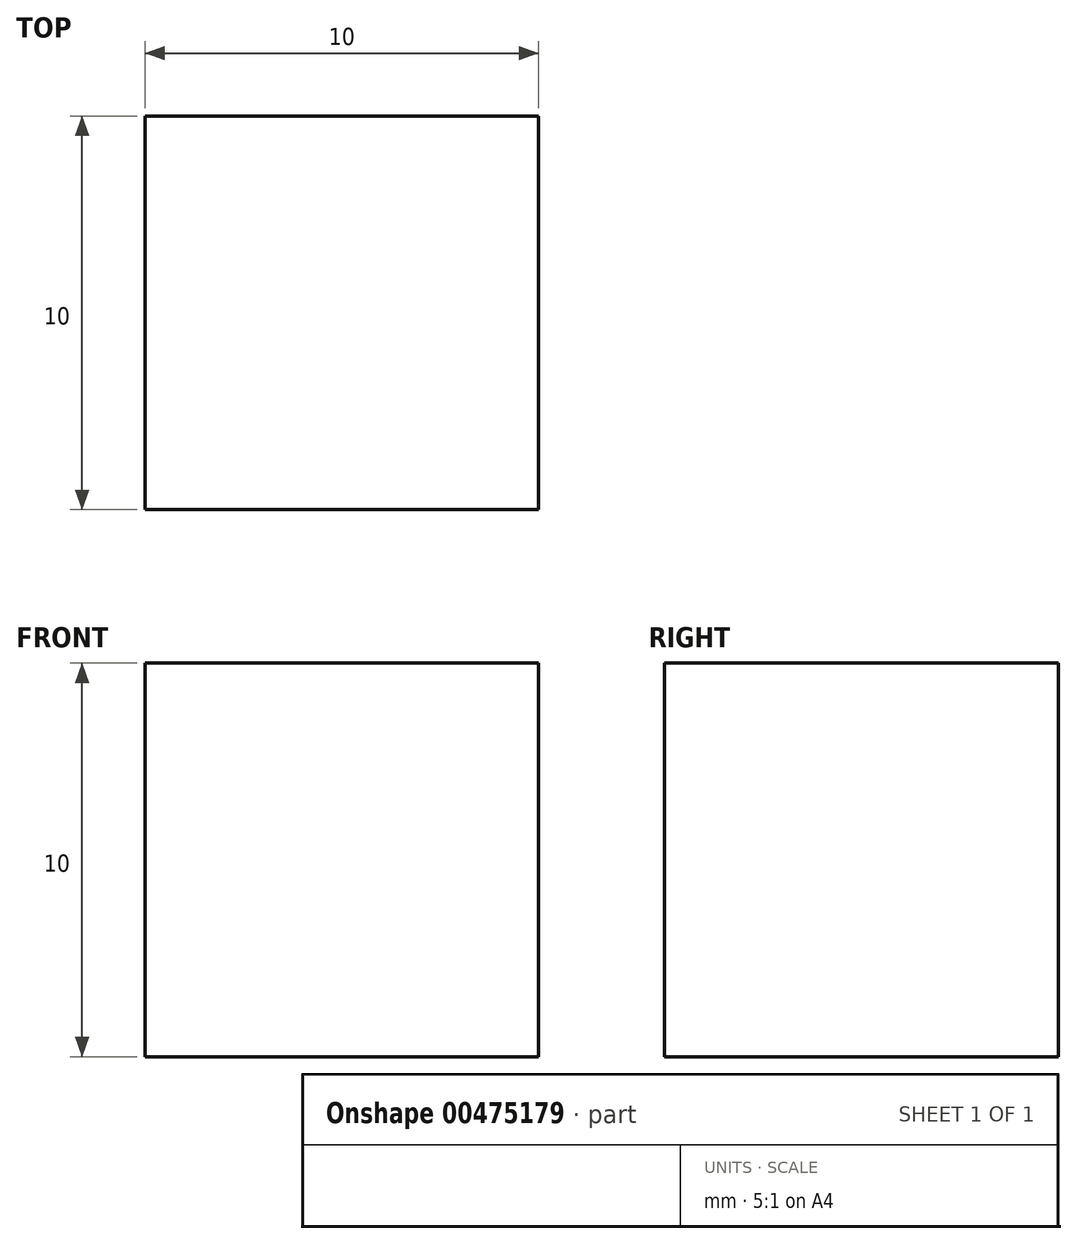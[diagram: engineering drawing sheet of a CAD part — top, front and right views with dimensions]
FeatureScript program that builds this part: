
annotation { "Feature Type Name" : "Feature", "Feature Type Description" : "" }
export const myFeature = defineFeature(function(context is Context, id is Id, definition is map)
    precondition{}
    {
        {
            var Q0;
            Q0=qCreatedBy(makeId("Top.planeOp"),FACE);
            var sketch = newSketch(context, id + "F0", { "sketchPlane" : qUnion([Q0])});
            skLineSegment(sketch, "E0.bottom", {"start": v(5, -5) * mm, "end": v(-5, -5) * mm});
            skLineSegment(sketch, "E0.top", {"start": v(5, 5) * mm, "end": v(-5, 5) * mm});
            skLineSegment(sketch, "E0.left", {"start": v(5, -5) * mm, "end": v(5, 5) * mm});
            skLineSegment(sketch, "E0.right", {"start": v(-5, -5) * mm, "end": v(-5, 5) * mm});
            skPoint(sketch, "E0.middle", {"position": v(0, 0) * mm});
            skSolve(sketch);
        }
        {
            var Q0;
            Q0 = qSketchRegion(id + "F0", true);
            extrude(context, id + "F1", {"entities" : qUnion([Q0]), "depth" : 10 * mm, "offsetDistance" : 25 * mm});
        }
    });
